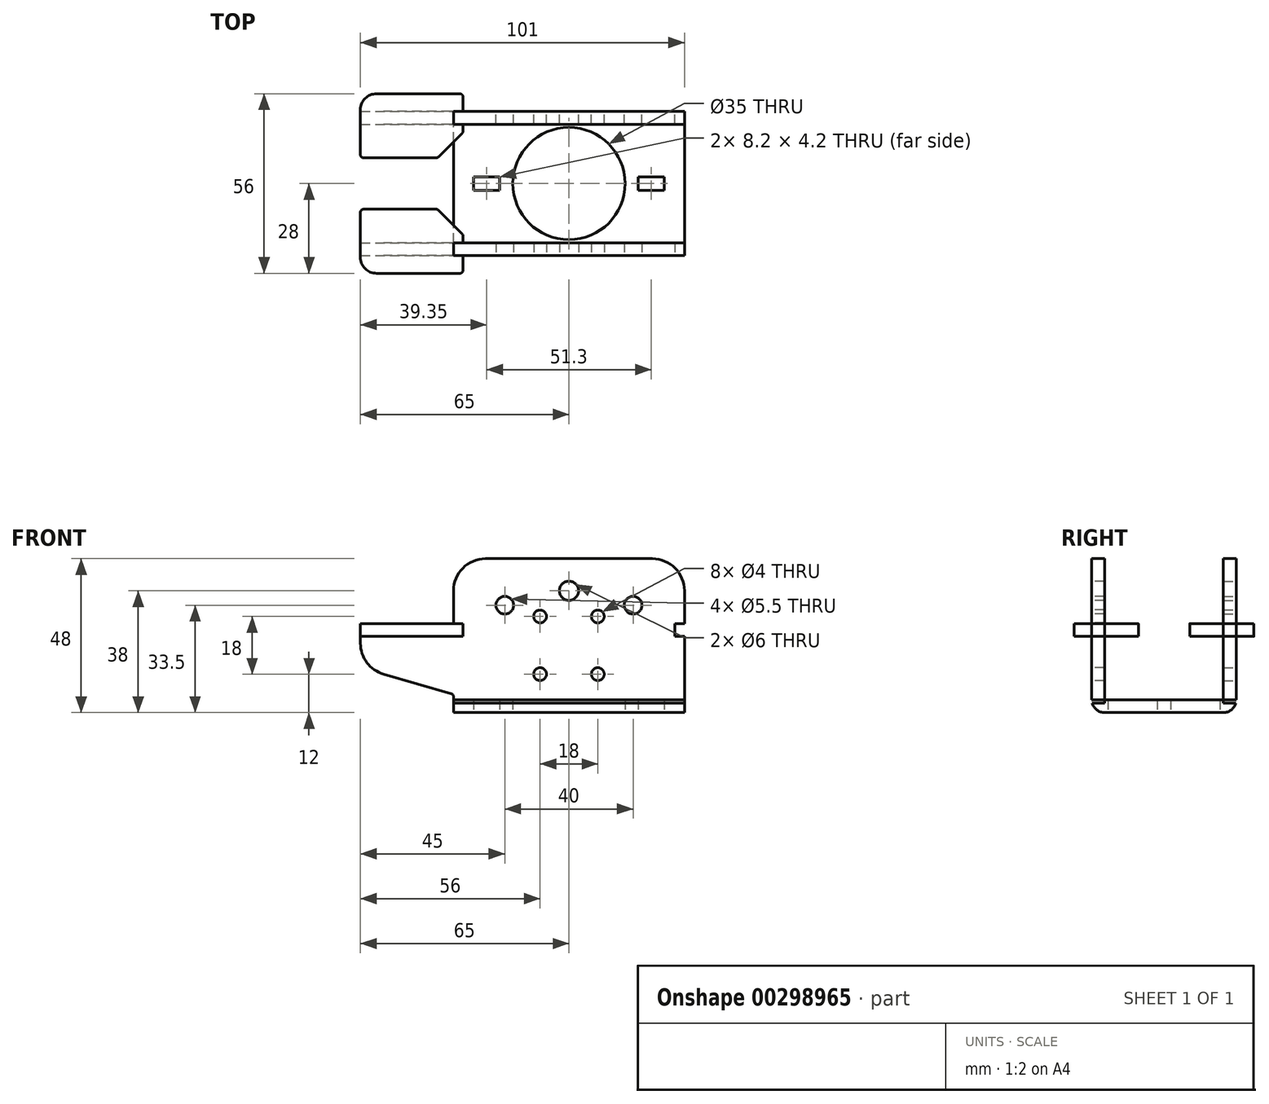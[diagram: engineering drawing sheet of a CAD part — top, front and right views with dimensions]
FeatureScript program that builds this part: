
annotation { "Feature Type Name" : "Feature", "Feature Type Description" : "" }
export const myFeature = defineFeature(function(context is Context, id is Id, definition is map)
    precondition{}
    {
        {
            var Q0;
            Q0=qCreatedBy(makeId("Front.planeOp"),FACE);
            var sketch = newSketch(context, id + "F0", { "sketchPlane" : qUnion([Q0])});
            skLineSegment(sketch, "E0.bottom", {"start": v(-36, 0) * mm, "end": v(36, 0) * mm});
            skLineSegment(sketch, "E0.top", {"start": v(-26, 48) * mm, "end": v(26, 48) * mm});
            skLineSegment(sketch, "E1.top", {"start": v(-36, 3) * mm, "end": v(36, 3) * mm});
            skLineSegment(sketch, "E1.left", {"start": v(-36, 0) * mm, "end": v(-36, 3) * mm});
            skLineSegment(sketch, "E1.right", {"start": v(36, 0) * mm, "end": v(36, 3) * mm});
            skLineSegment(sketch, "E2.top", {"start": v(36, 27.8) * mm, "end": v(65, 27.8) * mm});
            skArc(sketch, "E3", {"start": v(65, 21.61) * mm, "mid": v(62.99, 15.6) * mm, "end": v(57.76, 12) * mm});
            skArc(sketch, "E4", {"start": v(36, 5) * mm, "mid": v(36.2, 5.6) * mm, "end": v(36.72, 5.96) * mm});
            skLineSegment(sketch, "E5", {"start": v(36.72, 5.96) * mm, "end": v(57.76, 12) * mm});
            skLineSegment(sketch, "E6", {"start": v(65, 21.61) * mm, "end": v(65, 27.8) * mm});
            skLineSegment(sketch, "E7.MirrorCS", {"start": v(-36.72, 5.96) * mm, "end": v(-57.76, 12) * mm});
            skArc(sketch, "E8.MirrorCS", {"start": v(-65, 21.61) * mm, "mid": v(-62.99, 15.6) * mm, "end": v(-57.76, 12) * mm});
            skLineSegment(sketch, "E9.MirrorCS", {"start": v(-65, 21.61) * mm, "end": v(-65, 27.8) * mm});
            skLineSegment(sketch, "E10.MirrorCS", {"start": v(-36, 27.8) * mm, "end": v(-65, 27.8) * mm});
            skPoint(sketch, "E11.visualSharp", {"position": v(-36, 48) * mm});
            skArc(sketch, "E11.filletArc", {"start": v(-26, 48) * mm, "mid": v(-33.07, 45.07) * mm, "end": v(-36, 38) * mm});
            skPoint(sketch, "E12.visualSharp", {"position": v(36, 48) * mm});
            skArc(sketch, "E12.filletArc", {"start": v(36, 38) * mm, "mid": v(33.07, 45.07) * mm, "end": v(26, 48) * mm});
            skLineSegment(sketch, "E13.bottom", {"start": v(65, 27.8) * mm, "end": v(33, 27.8) * mm});
            skLineSegment(sketch, "E13.top", {"start": v(65, 23.8) * mm, "end": v(33, 23.8) * mm});
            skLineSegment(sketch, "E13.left", {"start": v(65, 27.8) * mm, "end": v(65, 23.8) * mm});
            skLineSegment(sketch, "E13.right", {"start": v(33, 27.8) * mm, "end": v(33, 23.8) * mm});
            skLineSegment(sketch, "E14.MirrorCS", {"start": v(-65, 27.8) * mm, "end": v(-33, 27.8) * mm});
            skLineSegment(sketch, "E15.MirrorCS", {"start": v(-65, 23.8) * mm, "end": v(-33, 23.8) * mm});
            skLineSegment(sketch, "E16.MirrorCS", {"start": v(-33, 27.8) * mm, "end": v(-33, 23.8) * mm});
            skArc(sketch, "E17.MirrorCS", {"start": v(-36, 5) * mm, "mid": v(-36.2, 5.6) * mm, "end": v(-36.72, 5.96) * mm});
            skCircle(sketch, "E18", {"center": v(9, 12) * mm, "radius": 2 * mm});
            skCircle(sketch, "E19", {"center": v(9, 30) * mm, "radius": 2 * mm});
            skCircle(sketch, "E20", {"center": v(20, 33.5) * mm, "radius": 2.75 * mm});
            skCircle(sketch, "E21.MirrorC", {"center": v(-9, 12) * mm, "radius": 2 * mm});
            skCircle(sketch, "E22.MirrorC", {"center": v(-9, 30) * mm, "radius": 2 * mm});
            skCircle(sketch, "E23.MirrorC", {"center": v(-20, 33.5) * mm, "radius": 2.75 * mm});
            skLineSegment(sketch, "E24", {"start": v(-36, 38) * mm, "end": v(-36, 27.8) * mm});
            skLineSegment(sketch, "E25", {"start": v(-36, 3) * mm, "end": v(-36, 23.8) * mm});
            skLineSegment(sketch, "E26", {"start": v(36, 38) * mm, "end": v(36, 27.8) * mm});
            skLineSegment(sketch, "E27", {"start": v(36, 3) * mm, "end": v(36, 23.8) * mm});
            skCircle(sketch, "E28", {"center": v(0, 38) * mm, "radius": 3 * mm});
            skSolve(sketch);
        }
        {
            var Q0;
            Q0=makeQuery(id+"F0.imprint","IMPRINT",FACE,{"disambiguationData":[TD([[makeQuery(id+"F0.imprint","IMPRINT",EDGE,{"derivedFrom":sQuery(id+"F0.wireOp",EDGE,"E0.top")}),-1.0]])]});
            var Q1;
            Q1=makeQuery(id+"F0.imprint","IMPRINT",FACE,{"disambiguationData":[TD([[makeQuery(id+"F0.imprint","IMPRINT",EDGE,{"derivedFrom":sQuery(id+"F0.wireOp",EDGE,"E3")}),-1.0]])]});
            var Q2;
            Q2=makeQuery(id+"F0.imprint","IMPRINT",FACE,{"disambiguationData":[TD([[makeQuery(id+"F0.imprint","IMPRINT",EDGE,{"derivedFrom":sQuery(id+"F0.wireOp",EDGE,"E7.MirrorCS")}),-1.0]])]});
            extrude(context, id + "F1", {"entities" : qUnion([Q0, Q1, Q2]), "depth" : 4 * mm});
        }
        {
            var Q0;
            {var subQ3=sQuery(id+"F0.wireOp",EDGE,"E13.left");Q0=makeQuery(id+"F0.imprint","IMPRINT",FACE,{"disambiguationData":[TD([[makeQuery(id+"F0.imprint","IMPRINT",EDGE,{"derivedFrom":subQ3}),-1.0]])]});}
            var Q1;
            {var subQ7=sQuery(id+"F0.wireOp",EDGE,"E16.MirrorCS");Q1=makeQuery(id+"F0.imprint","IMPRINT",FACE,{"disambiguationData":[TD([[makeQuery(id+"F0.imprint","IMPRINT",EDGE,{"derivedFrom":subQ7}),-1.0]])]});}
            extrude(context, id + "F2", {"entities" : qUnion([Q0, Q1]), "operationType" : NewBodyOperationType.ADD, "depth" : 14.5 * mm, "hasSecondDirection" : true, "secondDirectionOppositeDirection" : true, "secondDirectionDepth" : 5.5 * mm});
        }
        {
            var Q0;
            Q0=makeQuery(id+"F2.opExtrude","CAP_EDGE",EDGE,{"disambiguationData":[OSD([sQuery(id+"F0.wireOp",EDGE,"E9.MirrorCS")])],"isStart":true});
            var Q1;
            Q1=makeQuery(id+"F2.opExtrude","CAP_EDGE",EDGE,{"disambiguationData":[OSD([sQuery(id+"F0.wireOp",EDGE,"E13.left")])],"isStart":true});
            fillet(context, id + "F3", {"entities" : qUnion([Q0, Q1]), "radius" : 5 * mm, "tangentPropagation" : true, "allowEdgeOverflow" : false});
        }
        {
            var Q0;
            Q0=makeQuery(id+"F2.opExtrude","CAP_EDGE",EDGE,{"disambiguationData":[OSD([sQuery(id+"F0.wireOp",EDGE,"E9.MirrorCS")])],"isStart":false});
            var Q1;
            Q1=makeQuery(id+"F2.opExtrude","CAP_EDGE",EDGE,{"disambiguationData":[OSD([sQuery(id+"F0.wireOp",EDGE,"E16.MirrorCS")])],"isStart":true});
            var Q2;
            Q2=makeQuery(id+"F2.opExtrude","CAP_EDGE",EDGE,{"disambiguationData":[OSD([sQuery(id+"F0.wireOp",EDGE,"E13.left")])],"isStart":false});
            var Q3;
            Q3=makeQuery(id+"F2.opExtrude","CAP_EDGE",EDGE,{"disambiguationData":[OSD([sQuery(id+"F0.wireOp",EDGE,"E13.right")])],"isStart":true});
            fillet(context, id + "F4", {"entities" : qUnion([Q0, Q1, Q2, Q3]), "radius" : 1 * mm, "tangentPropagation" : true, "allowEdgeOverflow" : false});
        }
        {
            var Q0;
            Q0=makeQuery(id+"F2.opExtrude","CAP_EDGE",EDGE,{"disambiguationData":[OSD([sQuery(id+"F0.wireOp",EDGE,"E13.right")])],"isStart":false});
            var Q1;
            Q1=makeQuery(id+"F2.opExtrude","CAP_EDGE",EDGE,{"disambiguationData":[OSD([sQuery(id+"F0.wireOp",EDGE,"E16.MirrorCS")])],"isStart":false});
            chamfer(context, id + "F5", {"entities" : qUnion([Q0, Q1]), "width" : 8 * mm, "tangentPropagation" : true});
        }
        {
            var Q0;
            {var subQ0=sQuery(id+"F0.wireOp",EDGE,"E13.right");Q0=makeQuery(id+"F5.opChamfer","BLEND_EDGE",EDGE,{"blendedFrom":[makeQuery(id+"F2.opExtrude","CAP_EDGE",EDGE,{"disambiguationData":[OSD([subQ0])],"isStart":false}),makeQuery(id+"F2.opExtrude","CAP_FACE",FACE,{"disambiguationData":[OSD([sQuery(id+"F0.wireOp",EDGE,"E13.bottom"),sQuery(id+"F0.wireOp",EDGE,"E13.top"),sQuery(id+"F0.wireOp",EDGE,"E13.left"),subQ0])],"isStart":false})],"blendedInto":[makeQuery(id+"F2.opExtrude","CAP_FACE",FACE,{"disambiguationData":[OSD([sQuery(id+"F0.wireOp",EDGE,"E13.bottom"),sQuery(id+"F0.wireOp",EDGE,"E13.top"),sQuery(id+"F0.wireOp",EDGE,"E13.left"),subQ0])],"isStart":false})]});}
            var Q1;
            {var subQ0=sQuery(id+"F0.wireOp",EDGE,"E13.right");var subQ1=sQuery(id+"F0.wireOp",EDGE,"E13.top");var subQ2=sQuery(id+"F0.wireOp",EDGE,"E13.bottom");Q1=makeQuery(id+"F5.opChamfer","BLEND_EDGE",EDGE,{"blendedFrom":[makeQuery(id+"F2.opExtrude","CAP_EDGE",EDGE,{"disambiguationData":[OSD([subQ0])],"isStart":false}),makeQuery(id+"F2.boolean.opBoolean","SPLIT",FACE,{"disambiguationData":[TD([makeQuery(id+"F2.opExtrude","CAP_FACE",FACE,{"disambiguationData":[OSD([subQ2,subQ1,sQuery(id+"F0.wireOp",EDGE,"E13.left"),subQ0])],"isStart":false})])],"derivedFrom":makeQuery(id+"F2.opExtrude","SWEPT_FACE",FACE,{"disambiguationData":[OSD([subQ0])]})})],"blendedInto":[makeQuery(id+"F2.boolean.opBoolean","SPLIT",FACE,{"disambiguationData":[TD([makeQuery(id+"F2.opExtrude","CAP_FACE",FACE,{"disambiguationData":[OSD([subQ2,subQ1,sQuery(id+"F0.wireOp",EDGE,"E13.left"),subQ0])],"isStart":false})])],"derivedFrom":makeQuery(id+"F2.opExtrude","SWEPT_FACE",FACE,{"disambiguationData":[OSD([subQ0])]})})]});}
            var Q2;
            {var subQ0=sQuery(id+"F0.wireOp",EDGE,"E16.MirrorCS");var subQ1=sQuery(id+"F0.wireOp",EDGE,"E15.MirrorCS");var subQ2=sQuery(id+"F0.wireOp",EDGE,"E14.MirrorCS");var subQ3=sQuery(id+"F0.wireOp",EDGE,"E9.MirrorCS");Q2=makeQuery(id+"F5.opChamfer","BLEND_EDGE",EDGE,{"blendedFrom":[makeQuery(id+"F2.opExtrude","CAP_EDGE",EDGE,{"disambiguationData":[OSD([subQ0])],"isStart":false}),makeQuery(id+"F2.boolean.opBoolean","SPLIT",FACE,{"disambiguationData":[TD([makeQuery(id+"F2.opExtrude","CAP_FACE",FACE,{"disambiguationData":[OSD([subQ3,subQ2,subQ1,subQ0])],"isStart":false})])],"derivedFrom":makeQuery(id+"F2.opExtrude","SWEPT_FACE",FACE,{"disambiguationData":[OSD([subQ0])]})})],"blendedInto":[makeQuery(id+"F2.boolean.opBoolean","SPLIT",FACE,{"disambiguationData":[TD([makeQuery(id+"F2.opExtrude","CAP_FACE",FACE,{"disambiguationData":[OSD([subQ3,subQ2,subQ1,subQ0])],"isStart":false})])],"derivedFrom":makeQuery(id+"F2.opExtrude","SWEPT_FACE",FACE,{"disambiguationData":[OSD([subQ0])]})})]});}
            var Q3;
            {var subQ0=sQuery(id+"F0.wireOp",EDGE,"E16.MirrorCS");Q3=makeQuery(id+"F5.opChamfer","BLEND_EDGE",EDGE,{"blendedFrom":[makeQuery(id+"F2.opExtrude","CAP_EDGE",EDGE,{"disambiguationData":[OSD([subQ0])],"isStart":false}),makeQuery(id+"F2.opExtrude","CAP_FACE",FACE,{"disambiguationData":[OSD([sQuery(id+"F0.wireOp",EDGE,"E9.MirrorCS"),sQuery(id+"F0.wireOp",EDGE,"E14.MirrorCS"),sQuery(id+"F0.wireOp",EDGE,"E15.MirrorCS"),subQ0])],"isStart":false})],"blendedInto":[makeQuery(id+"F2.opExtrude","CAP_FACE",FACE,{"disambiguationData":[OSD([sQuery(id+"F0.wireOp",EDGE,"E9.MirrorCS"),sQuery(id+"F0.wireOp",EDGE,"E14.MirrorCS"),sQuery(id+"F0.wireOp",EDGE,"E15.MirrorCS"),subQ0])],"isStart":false})]});}
            fillet(context, id + "F6", {"entities" : qUnion([Q0, Q1, Q2, Q3]), "radius" : 1 * mm, "tangentPropagation" : true, "allowEdgeOverflow" : false});
        }
        {
            var Q0;
            Q0=makeQuery(id+"F1.opExtrude","SWEPT_BODY",BODY,{"disambiguationData":[OSD([sQuery(id+"F0.wireOp",EDGE,"E0.top"),sQuery(id+"F0.wireOp",EDGE,"E1.top"),sQuery(id+"F0.wireOp",EDGE,"E3"),sQuery(id+"F0.wireOp",EDGE,"E4"),sQuery(id+"F0.wireOp",EDGE,"E5"),sQuery(id+"F0.wireOp",EDGE,"E6"),sQuery(id+"F0.wireOp",EDGE,"E7.MirrorCS"),sQuery(id+"F0.wireOp",EDGE,"E8.MirrorCS"),sQuery(id+"F0.wireOp",EDGE,"E9.MirrorCS"),sQuery(id+"F0.wireOp",EDGE,"E11.filletArc"),sQuery(id+"F0.wireOp",EDGE,"E12.filletArc"),sQuery(id+"F0.wireOp",EDGE,"E13.bottom"),sQuery(id+"F0.wireOp",EDGE,"E13.top"),sQuery(id+"F0.wireOp",EDGE,"E13.right"),sQuery(id+"F0.wireOp",EDGE,"E14.MirrorCS"),sQuery(id+"F0.wireOp",EDGE,"E15.MirrorCS"),sQuery(id+"F0.wireOp",EDGE,"E16.MirrorCS"),sQuery(id+"F0.wireOp",EDGE,"E17.MirrorCS"),sQuery(id+"F0.wireOp",EDGE,"E18"),sQuery(id+"F0.wireOp",EDGE,"E19"),sQuery(id+"F0.wireOp",EDGE,"E20"),sQuery(id+"F0.wireOp",EDGE,"E21.MirrorC"),sQuery(id+"F0.wireOp",EDGE,"E22.MirrorC"),sQuery(id+"F0.wireOp",EDGE,"E23.MirrorC"),sQuery(id+"F0.wireOp",EDGE,"E24"),sQuery(id+"F0.wireOp",EDGE,"E25"),sQuery(id+"F0.wireOp",EDGE,"E26"),sQuery(id+"F0.wireOp",EDGE,"E27")])]});
            var Q1;
            Q1=qCreatedBy(makeId("Front.planeOp"),FACE);
            transform(context, id + "F7", {"entities" : qUnion([Q0]), "transformType" : TransformType.TRANSLATION_DISTANCE, "transformDirection" : qUnion([Q1]), "distance" : 22.5 * mm, "oppositeDirection" : true, "makeCopy" : false});
        }
        {
            var Q0;
            Q0=makeQuery(id+"F1.opExtrude","SWEPT_BODY",BODY,{"disambiguationData":[OSD([sQuery(id+"F0.wireOp",EDGE,"E0.top"),sQuery(id+"F0.wireOp",EDGE,"E1.top"),sQuery(id+"F0.wireOp",EDGE,"E3"),sQuery(id+"F0.wireOp",EDGE,"E4"),sQuery(id+"F0.wireOp",EDGE,"E5"),sQuery(id+"F0.wireOp",EDGE,"E6"),sQuery(id+"F0.wireOp",EDGE,"E7.MirrorCS"),sQuery(id+"F0.wireOp",EDGE,"E8.MirrorCS"),sQuery(id+"F0.wireOp",EDGE,"E9.MirrorCS"),sQuery(id+"F0.wireOp",EDGE,"E11.filletArc"),sQuery(id+"F0.wireOp",EDGE,"E12.filletArc"),sQuery(id+"F0.wireOp",EDGE,"E13.bottom"),sQuery(id+"F0.wireOp",EDGE,"E13.top"),sQuery(id+"F0.wireOp",EDGE,"E13.right"),sQuery(id+"F0.wireOp",EDGE,"E14.MirrorCS"),sQuery(id+"F0.wireOp",EDGE,"E15.MirrorCS"),sQuery(id+"F0.wireOp",EDGE,"E16.MirrorCS"),sQuery(id+"F0.wireOp",EDGE,"E17.MirrorCS"),sQuery(id+"F0.wireOp",EDGE,"E18"),sQuery(id+"F0.wireOp",EDGE,"E19"),sQuery(id+"F0.wireOp",EDGE,"E20"),sQuery(id+"F0.wireOp",EDGE,"E21.MirrorC"),sQuery(id+"F0.wireOp",EDGE,"E22.MirrorC"),sQuery(id+"F0.wireOp",EDGE,"E23.MirrorC"),sQuery(id+"F0.wireOp",EDGE,"E24"),sQuery(id+"F0.wireOp",EDGE,"E25"),sQuery(id+"F0.wireOp",EDGE,"E26"),sQuery(id+"F0.wireOp",EDGE,"E27")])]});
            var Q1;
            Q1=qCreatedBy(makeId("Front.planeOp"),FACE);
            mirror(context, id + "F8", {"entities" : qUnion([Q0]), "mirrorPlane" : qUnion([Q1])});
        }
        {
            var Q0;
            Q0=qCreatedBy(makeId("Top.planeOp"),FACE);
            var sketch = newSketch(context, id + "F9", { "sketchPlane" : qUnion([Q0])});
            skLineSegment(sketch, "E29.bottom", {"start": v(36, -22.5) * mm, "end": v(-36, -22.5) * mm});
            skLineSegment(sketch, "E29.top", {"start": v(36, 22.5) * mm, "end": v(-36, 22.5) * mm});
            skLineSegment(sketch, "E29.left", {"start": v(36, -22.5) * mm, "end": v(36, 22.5) * mm});
            skLineSegment(sketch, "E29.right", {"start": v(-36, -22.5) * mm, "end": v(-36, 22.5) * mm});
            skPoint(sketch, "E29.middle", {"position": v(0, 0) * mm});
            skCircle(sketch, "E30", {"center": v(0, 0) * mm, "radius": 17.5 * mm});
            skLineSegment(sketch, "E31.bottom", {"start": v(-21.55, -2.1) * mm, "end": v(-29.75, -2.1) * mm});
            skLineSegment(sketch, "E31.top", {"start": v(-21.55, 2.1) * mm, "end": v(-29.75, 2.1) * mm});
            skLineSegment(sketch, "E31.left", {"start": v(-21.55, -2.1) * mm, "end": v(-21.55, 2.1) * mm});
            skLineSegment(sketch, "E31.right", {"start": v(-29.75, -2.1) * mm, "end": v(-29.75, 2.1) * mm});
            skPoint(sketch, "E31.middle", {"position": v(-25.65, 0) * mm});
            skLineSegment(sketch, "E32.MirrorCS", {"start": v(21.55, 2.1) * mm, "end": v(29.75, 2.1) * mm});
            skLineSegment(sketch, "E33.MirrorCS", {"start": v(21.55, -2.1) * mm, "end": v(29.75, -2.1) * mm});
            skLineSegment(sketch, "E34.MirrorCS", {"start": v(21.55, -2.1) * mm, "end": v(21.55, 2.1) * mm});
            skLineSegment(sketch, "E35.MirrorCS", {"start": v(29.75, -2.1) * mm, "end": v(29.75, 2.1) * mm});
            skSolve(sketch);
        }
        {
            var Q0;
            Q0=makeQuery(id+"F9.imprint","IMPRINT",FACE,{"disambiguationData":[TD([[makeQuery(id+"F9.imprint","IMPRINT",EDGE,{"derivedFrom":sQuery(id+"F9.wireOp",EDGE,"E29.bottom")}),-1.0]])]});
            extrude(context, id + "F10", {"entities" : qUnion([Q0]), "depth" : 4 * mm});
        }
        {
            var Q0;
            Q0=makeQuery(id+"F10.opExtrude","CAP_EDGE",EDGE,{"disambiguationData":[OSD([sQuery(id+"F9.wireOp",EDGE,"E29.top")])],"isStart":true});
            var Q1;
            Q1=makeQuery(id+"F10.opExtrude","CAP_EDGE",EDGE,{"disambiguationData":[OSD([sQuery(id+"F9.wireOp",EDGE,"E29.bottom")])],"isStart":true});
            fillet(context, id + "F11", {"entities" : qUnion([Q0, Q1]), "radius" : 4 * mm, "tangentPropagation" : true, "allowEdgeOverflow" : false});
        }
        {
            var Q0;
            Q0=makeQuery(id+"F1.opExtrude","SWEPT_FACE",FACE,{"disambiguationData":[OSD([sQuery(id+"F0.wireOp",EDGE,"E1.top")])]});
            extrude(context, id + "F12", {"entities" : qUnion([Q0]), "operationType" : NewBodyOperationType.REMOVE, "oppositeDirection" : true, "depth" : 1 * mm});
        }
        {
            var Q0;
            Q0=makeQuery(id+"F8.opPattern","COPY",FACE,{"derivedFrom":makeQuery(id+"F1.opExtrude","SWEPT_FACE",FACE,{"disambiguationData":[OSD([sQuery(id+"F0.wireOp",EDGE,"E1.top")])]}),"instanceName":"1"});
            extrude(context, id + "F13", {"entities" : qUnion([Q0]), "operationType" : NewBodyOperationType.REMOVE, "oppositeDirection" : true, "depth" : 1 * mm});
        }
    });
